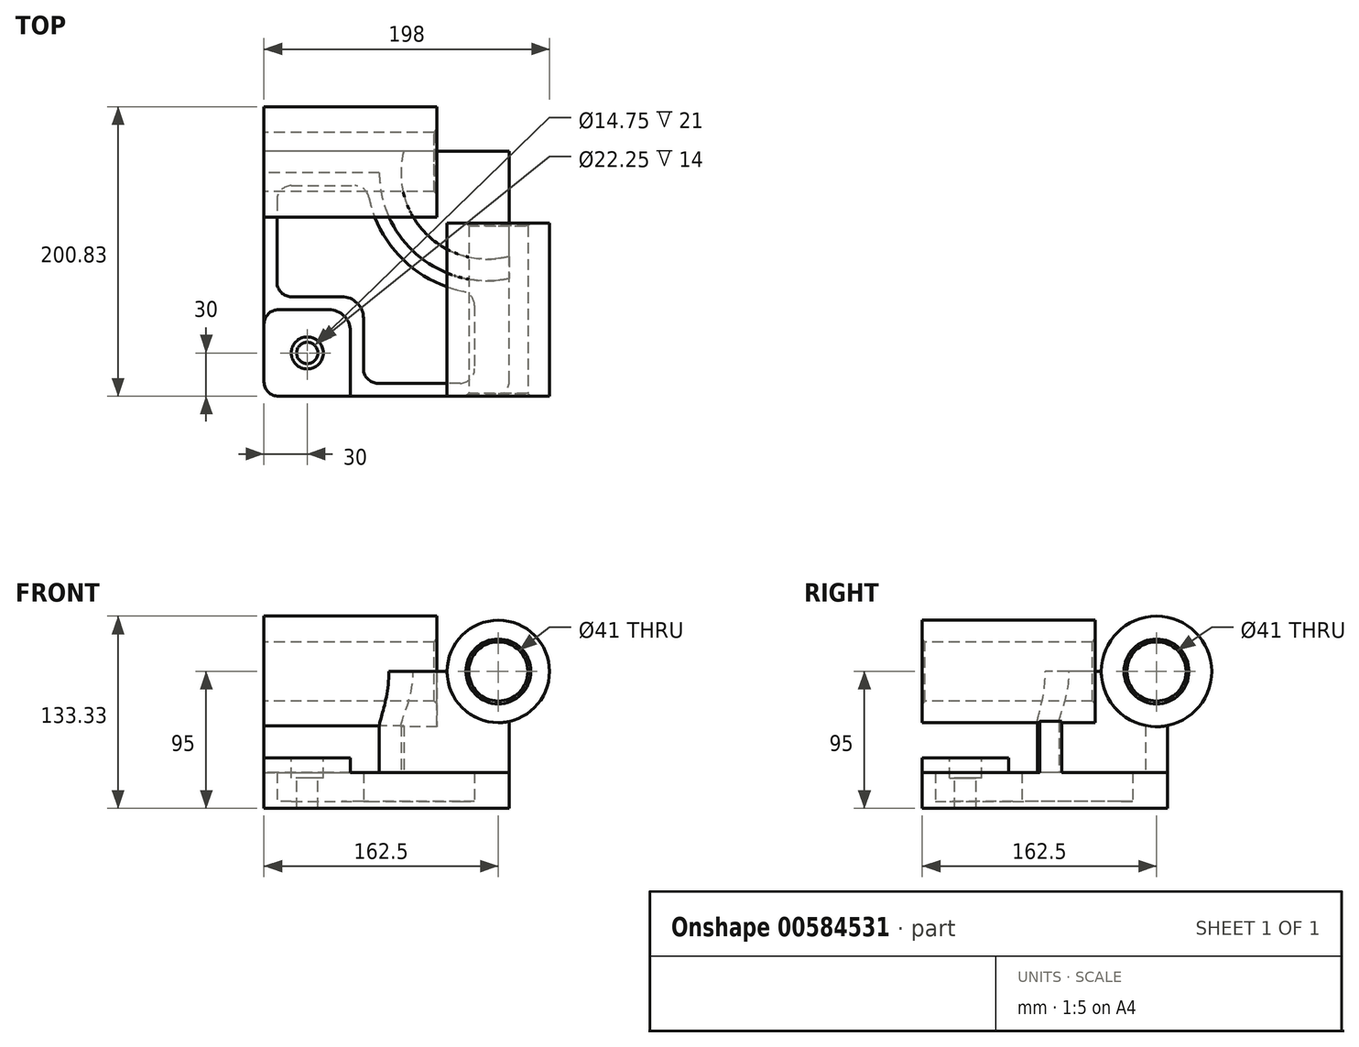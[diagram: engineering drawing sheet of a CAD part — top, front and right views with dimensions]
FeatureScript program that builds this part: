
annotation { "Feature Type Name" : "Feature", "Feature Type Description" : "" }
export const myFeature = defineFeature(function(context is Context, id is Id, definition is map)
    precondition{}
    {
        {
            var Q0;
            Q0=qCreatedBy(makeId("Top.planeOp"),FACE);
            var sketch = newSketch(context, id + "F0", { "sketchPlane" : qUnion([Q0])});
            skLineSegment(sketch, "E0", {"start": v(0, 0) * mm, "end": v(213, 0) * mm});
            skLineSegment(sketch, "E1", {"start": v(213, 0) * mm, "end": v(213, 200) * mm});
            skLineSegment(sketch, "E2", {"start": v(213, 200) * mm, "end": v(0, 200) * mm});
            skLineSegment(sketch, "E3", {"start": v(0, 200) * mm, "end": v(0, 0) * mm});
            skLineSegment(sketch, "E4", {"start": v(0, 0) * mm, "end": v(60, 0) * mm});
            skLineSegment(sketch, "E5", {"start": v(60, 0) * mm, "end": v(60, 60) * mm});
            skLineSegment(sketch, "E6", {"start": v(60, 60) * mm, "end": v(0, 60) * mm});
            skLineSegment(sketch, "E7", {"start": v(0, 0) * mm, "end": v(170, 0) * mm});
            skLineSegment(sketch, "E8", {"start": v(170, 0) * mm, "end": v(170, 170) * mm});
            skLineSegment(sketch, "E9", {"start": v(170, 170) * mm, "end": v(0, 170) * mm});
            skLineSegment(sketch, "E10", {"start": v(170, 0) * mm, "end": v(155, 0) * mm});
            skLineSegment(sketch, "E11", {"start": v(155, 0) * mm, "end": v(155, 80) * mm});
            skLineSegment(sketch, "E12", {"start": v(0, 155) * mm, "end": v(80, 155) * mm});
            skLineSegment(sketch, "E13", {"start": v(9, 146) * mm, "end": v(71.48, 146) * mm});
            skLineSegment(sketch, "E14", {"start": v(146, 71.48) * mm, "end": v(146, 9) * mm});
            skLineSegment(sketch, "E15", {"start": v(146, 9) * mm, "end": v(69, 9) * mm});
            skLineSegment(sketch, "E16", {"start": v(69, 9) * mm, "end": v(69, 69) * mm});
            skLineSegment(sketch, "E17", {"start": v(9, 146) * mm, "end": v(9, 69) * mm});
            skLineSegment(sketch, "E18", {"start": v(9, 69) * mm, "end": v(69, 69) * mm});
            skArc(sketch, "E19", {"start": v(80, 155) * mm, "mid": v(107.57, 96.9) * mm, "end": v(170, 81.52) * mm});
            skArc(sketch, "E20", {"start": v(71.48, 146) * mm, "mid": v(95.6, 95.6) * mm, "end": v(146, 71.48) * mm});
            skArc(sketch, "E21", {"start": v(96.9, 170) * mm, "mid": v(112.57, 112.57) * mm, "end": v(170, 96.9) * mm});
            skSolve(sketch);
        }
        {
            var Q0;
            {var subQ4=sQuery(id+"F0.wireOp",EDGE,"E5");Q0=makeQuery(id+"F0.imprint","IMPRINT",FACE,{"disambiguationData":[TD([[makeQuery(id+"F0.imprint","IMPRINT",EDGE,{"derivedFrom":subQ4}),1.0]])]});}
            extrude(context, id + "F1", {"entities" : qUnion([Q0]), "depth" : 35 * mm, "offsetDistance" : 25 * mm});
        }
        {
            var Q0;
            {var subQ6=sQuery(id+"F0.wireOp",EDGE,"E5");Q0=makeQuery(id+"F0.imprint","IMPRINT",FACE,{"disambiguationData":[TD([[makeQuery(id+"F0.imprint","IMPRINT",EDGE,{"derivedFrom":subQ6}),-1.0]])]});}
            extrude(context, id + "F2", {"entities" : qUnion([Q0]), "operationType" : NewBodyOperationType.ADD, "depth" : 25 * mm, "offsetDistance" : 25 * mm});
        }
        {
            var Q0;
            {var subQ0=sQuery(id+"F0.wireOp",EDGE,"E12");Q0=makeQuery(id+"F0.imprint","IMPRINT",FACE,{"disambiguationData":[TD([[makeQuery(id+"F0.imprint","IMPRINT",EDGE,{"derivedFrom":subQ0}),1.0]])]});}
            var Q1;
            {var subQ0=sQuery(id+"F0.wireOp",EDGE,"E10");Q1=makeQuery(id+"F0.imprint","IMPRINT",FACE,{"disambiguationData":[TD([[makeQuery(id+"F0.imprint","IMPRINT",EDGE,{"derivedFrom":subQ0}),-1.0]])]});}
            extrude(context, id + "F3", {"entities" : qUnion([Q0, Q1]), "operationType" : NewBodyOperationType.ADD, "depth" : 95 * mm, "offsetDistance" : 25 * mm});
        }
        {
            var Q0;
            Q0=makeQuery(id+"F0.imprint","IMPRINT",FACE,{"disambiguationData":[TD([[makeQuery(id+"F0.imprint","IMPRINT",EDGE,{"derivedFrom":sQuery(id+"F0.wireOp",EDGE,"E13")}),-1.0]])]});
            extrude(context, id + "F4", {"entities" : qUnion([Q0]), "operationType" : NewBodyOperationType.ADD, "depth" : 5 * mm, "offsetDistance" : 25 * mm});
        }
        {
            var Q0;
            {var subQ10=sQuery(id+"F0.wireOp",EDGE,"E0");Q0=makeQuery(id+"F0.imprint","IMPRINT",FACE,{"disambiguationData":[TD([[makeQuery(id+"F0.imprint","IMPRINT",EDGE,{"derivedFrom":subQ10}),1.0]])]});}
            var Q1;
            {var subQ3=sQuery(id+"F0.wireOp",EDGE,"E21");Q1=makeQuery(id+"F0.imprint","IMPRINT",FACE,{"disambiguationData":[TD([[makeQuery(id+"F0.imprint","IMPRINT",EDGE,{"derivedFrom":subQ3}),1.0]])]});}
            extrude(context, id + "F5", {"entities" : qUnion([Q0, Q1]), "operationType" : NewBodyOperationType.ADD, "depth" : 25 * mm, "offsetDistance" : 25 * mm});
        }
        {
            var Q0;
            Q0=qCreatedBy(makeId("Front.planeOp"),FACE);
            var sketch = newSketch(context, id + "F6", { "sketchPlane" : qUnion([Q0])});
            skLineSegment(sketch, "E22.0.0", {"start": v(0, 0) * mm, "end": v(213, 0) * mm});
            skLineSegment(sketch, "E22.0.1", {"start": v(213, 0) * mm, "end": v(213, 25) * mm});
            skLineSegment(sketch, "E22.0.2", {"start": v(213, 25) * mm, "end": v(170, 25) * mm});
            skLineSegment(sketch, "E22.0.3", {"start": v(170, 25) * mm, "end": v(170, 95) * mm});
            skLineSegment(sketch, "E22.0.4", {"start": v(170, 95) * mm, "end": v(155, 95) * mm});
            skLineSegment(sketch, "E22.0.5", {"start": v(155, 95) * mm, "end": v(155, 25) * mm});
            skLineSegment(sketch, "E22.0.6", {"start": v(155, 25) * mm, "end": v(60, 25) * mm});
            skLineSegment(sketch, "E22.0.7", {"start": v(60, 25) * mm, "end": v(60, 35) * mm});
            skLineSegment(sketch, "E22.0.8", {"start": v(60, 35) * mm, "end": v(0, 35) * mm});
            skLineSegment(sketch, "E22.0.9", {"start": v(0, 35) * mm, "end": v(0, 0) * mm});
            skPoint(sketch, "E23", {"position": v(162.5, 95) * mm});
            skCircle(sketch, "E24", {"center": v(162.5, 95) * mm, "radius": 20.5 * mm});
            skCircle(sketch, "E25", {"center": v(162.5, 95) * mm, "radius": 35.5 * mm});
            skSolve(sketch);
        }
        {
            var Q0;
            {var subQ0=sQuery(id+"F6.wireOp",EDGE,"E25");var subQ1=sQuery(id+"F6.wireOp",EDGE,"E22.0.3");var subQ2=makeQuery(id+"F6.imprint","INTERSECT",VERTEX,{"derivedFrom":[subQ1,subQ0]});Q0=makeQuery(id+"F6.imprint","IMPRINT",FACE,{"disambiguationData":[TD([[makeQuery(id+"F6.imprint","IMPRINT",EDGE,{"disambiguationData":[TD([[subQ2,-1.0]])],"derivedFrom":subQ1}),-1.0]])]});}
            var Q1;
            {var subQ0=sQuery(id+"F6.wireOp",EDGE,"E25");var subQ1=sQuery(id+"F6.wireOp",EDGE,"E22.0.3");var subQ2=makeQuery(id+"F6.imprint","INTERSECT",VERTEX,{"derivedFrom":[subQ1,subQ0]});Q1=makeQuery(id+"F6.imprint","IMPRINT",FACE,{"disambiguationData":[TD([[makeQuery(id+"F6.imprint","IMPRINT",EDGE,{"disambiguationData":[TD([[subQ2,-1.0]])],"derivedFrom":subQ1}),1.0]])]});}
            extrude(context, id + "F7", {"entities" : qUnion([Q0, Q1]), "operationType" : NewBodyOperationType.ADD, "oppositeDirection" : true, "depth" : 120 * mm, "offsetDistance" : 25 * mm});
        }
        {
            var Q0;
            {var subQ0=sQuery(id+"F6.wireOp",EDGE,"E22.0.4");Q0=makeQuery(id+"F6.imprint","IMPRINT",FACE,{"disambiguationData":[TD([[makeQuery(id+"F6.imprint","IMPRINT",EDGE,{"derivedFrom":subQ0}),-1.0]])]});}
            var Q1;
            {var subQ0=sQuery(id+"F6.wireOp",EDGE,"E22.0.4");Q1=makeQuery(id+"F6.imprint","IMPRINT",FACE,{"disambiguationData":[TD([[makeQuery(id+"F6.imprint","IMPRINT",EDGE,{"derivedFrom":subQ0}),1.0]])]});}
            extrude(context, id + "F8", {"entities" : qUnion([Q0, Q1]), "operationType" : NewBodyOperationType.REMOVE, "oppositeDirection" : true, "depth" : 120 * mm, "offsetDistance" : 25 * mm});
        }
        {
            var Q0;
            Q0=qCreatedBy(makeId("Right.planeOp"),FACE);
            var sketch = newSketch(context, id + "F9", { "sketchPlane" : qUnion([Q0])});
            skLineSegment(sketch, "E26.0.0", {"start": v(200, 0) * mm, "end": v(0, 0) * mm});
            skLineSegment(sketch, "E26.0.1", {"start": v(0, 0) * mm, "end": v(0, 35) * mm});
            skLineSegment(sketch, "E26.0.2", {"start": v(0, 35) * mm, "end": v(60, 35) * mm});
            skLineSegment(sketch, "E26.0.3", {"start": v(60, 35) * mm, "end": v(60, 25) * mm});
            skLineSegment(sketch, "E26.0.4", {"start": v(60, 25) * mm, "end": v(155, 25) * mm});
            skLineSegment(sketch, "E26.0.5", {"start": v(155, 25) * mm, "end": v(155, 95) * mm});
            skLineSegment(sketch, "E26.0.6", {"start": v(155, 95) * mm, "end": v(170, 95) * mm});
            skLineSegment(sketch, "E26.0.7", {"start": v(170, 95) * mm, "end": v(170, 25) * mm});
            skLineSegment(sketch, "E26.0.8", {"start": v(170, 25) * mm, "end": v(200, 25) * mm});
            skLineSegment(sketch, "E26.0.9", {"start": v(200, 25) * mm, "end": v(200, 0) * mm});
            skPoint(sketch, "E27", {"position": v(162.5, 95) * mm});
            skCircle(sketch, "E28", {"center": v(162.5, 95) * mm, "radius": 20.5 * mm});
            skCircle(sketch, "E29", {"center": v(162.5, 95) * mm, "radius": 38.33 * mm});
            skSolve(sketch);
        }
        {
            var Q0;
            {var subQ0=sQuery(id+"F9.wireOp",EDGE,"E29");var subQ1=sQuery(id+"F9.wireOp",EDGE,"E26.0.5");var subQ2=makeQuery(id+"F9.imprint","INTERSECT",VERTEX,{"derivedFrom":[subQ1,subQ0]});Q0=makeQuery(id+"F9.imprint","IMPRINT",FACE,{"disambiguationData":[TD([[makeQuery(id+"F9.imprint","IMPRINT",EDGE,{"disambiguationData":[TD([[subQ2,-1.0]])],"derivedFrom":subQ1}),1.0]])]});}
            var Q1;
            {var subQ0=sQuery(id+"F9.wireOp",EDGE,"E29");var subQ1=sQuery(id+"F9.wireOp",EDGE,"E26.0.5");var subQ2=makeQuery(id+"F9.imprint","INTERSECT",VERTEX,{"derivedFrom":[subQ1,subQ0]});Q1=makeQuery(id+"F9.imprint","IMPRINT",FACE,{"disambiguationData":[TD([[makeQuery(id+"F9.imprint","IMPRINT",EDGE,{"disambiguationData":[TD([[subQ2,-1.0]])],"derivedFrom":subQ1}),-1.0]])]});}
            extrude(context, id + "F10", {"entities" : qUnion([Q0, Q1]), "operationType" : NewBodyOperationType.ADD, "depth" : 120 * mm, "offsetDistance" : 25 * mm});
        }
        {
            var Q0;
            {var subQ0=sQuery(id+"F9.wireOp",EDGE,"E26.0.6");Q0=makeQuery(id+"F9.imprint","IMPRINT",FACE,{"disambiguationData":[TD([[makeQuery(id+"F9.imprint","IMPRINT",EDGE,{"derivedFrom":subQ0}),1.0]])]});}
            var Q1;
            {var subQ0=sQuery(id+"F9.wireOp",EDGE,"E26.0.6");Q1=makeQuery(id+"F9.imprint","IMPRINT",FACE,{"disambiguationData":[TD([[makeQuery(id+"F9.imprint","IMPRINT",EDGE,{"derivedFrom":subQ0}),-1.0]])]});}
            extrude(context, id + "F11", {"entities" : qUnion([Q0, Q1]), "operationType" : NewBodyOperationType.REMOVE, "depth" : 120 * mm, "offsetDistance" : 25 * mm});
        }
        {
            var Q0;
            Q0=makeQuery(id+"F5.opExtrude","SWEPT_EDGE",EDGE,{"disambiguationData":[OSD([sQuery(id+"F0.wireOp",EDGE,"E0"),sQuery(id+"F0.wireOp",EDGE,"E1")])]});
            var Q1;
            Q1=makeQuery(id+"F5.opExtrude","SWEPT_EDGE",EDGE,{"disambiguationData":[OSD([sQuery(id+"F0.wireOp",EDGE,"E1"),sQuery(id+"F0.wireOp",EDGE,"E2")])]});
            var Q2;
            Q2=makeQuery(id+"F5.opExtrude","SWEPT_EDGE",EDGE,{"disambiguationData":[OSD([sQuery(id+"F0.wireOp",EDGE,"E2"),sQuery(id+"F0.wireOp",EDGE,"E3")])]});
            var Q3;
            Q3=makeQuery(id+"F1.opExtrude","SWEPT_EDGE",EDGE,{"disambiguationData":[OSD([sQuery(id+"F0.wireOp",EDGE,"E3"),sQuery(id+"F0.wireOp",EDGE,"E7")])]});
            fillet(context, id + "F12", {"entities" : qUnion([Q0, Q1, Q2, Q3]), "radius" : 10 * mm, "tangentPropagation" : true, "allowEdgeOverflow" : false});
        }
        {
            var Q0;
            Q0=makeQuery(id+"F1.opExtrude","SWEPT_EDGE",EDGE,{"disambiguationData":[OSD([sQuery(id+"F0.wireOp",EDGE,"E5"),sQuery(id+"F0.wireOp",EDGE,"E6")])]});
            var Q1;
            Q1=makeQuery(id+"F2.opExtrude","SWEPT_EDGE",EDGE,{"disambiguationData":[OSD([sQuery(id+"F0.wireOp",EDGE,"E16"),sQuery(id+"F0.wireOp",EDGE,"E18")])]});
            fillet(context, id + "F13", {"entities" : qUnion([Q0, Q1]), "radius" : 15 * mm, "tangentPropagation" : true, "allowEdgeOverflow" : false});
        }
        {
            var Q0;
            Q0=makeQuery(id+"F2.opExtrude","SWEPT_EDGE",EDGE,{"disambiguationData":[OSD([sQuery(id+"F0.wireOp",EDGE,"E13"),sQuery(id+"F0.wireOp",EDGE,"E20")])]});
            var Q1;
            Q1=makeQuery(id+"F2.opExtrude","SWEPT_EDGE",EDGE,{"disambiguationData":[OSD([sQuery(id+"F0.wireOp",EDGE,"E13"),sQuery(id+"F0.wireOp",EDGE,"E17")])]});
            var Q2;
            Q2=makeQuery(id+"F2.opExtrude","SWEPT_EDGE",EDGE,{"disambiguationData":[OSD([sQuery(id+"F0.wireOp",EDGE,"E17"),sQuery(id+"F0.wireOp",EDGE,"E18")])]});
            var Q3;
            Q3=makeQuery(id+"F2.opExtrude","SWEPT_EDGE",EDGE,{"disambiguationData":[OSD([sQuery(id+"F0.wireOp",EDGE,"E15"),sQuery(id+"F0.wireOp",EDGE,"E16")])]});
            var Q4;
            Q4=makeQuery(id+"F2.opExtrude","SWEPT_EDGE",EDGE,{"disambiguationData":[OSD([sQuery(id+"F0.wireOp",EDGE,"E14"),sQuery(id+"F0.wireOp",EDGE,"E20")])]});
            var Q5;
            Q5=makeQuery(id+"F2.opExtrude","SWEPT_EDGE",EDGE,{"disambiguationData":[OSD([sQuery(id+"F0.wireOp",EDGE,"E14"),sQuery(id+"F0.wireOp",EDGE,"E15")])]});
            fillet(context, id + "F14", {"entities" : qUnion([Q0, Q1, Q2, Q3, Q4, Q5]), "radius" : 10 * mm, "tangentPropagation" : true, "allowEdgeOverflow" : false});
        }
        {
            var Q0;
            Q0=qCreatedBy(makeId("Top.planeOp"),FACE);
            cPlane(context, id + "F15", {"entities" : qUnion([Q0]), "cplaneType" : CPlaneType.OFFSET, "offset" : 35 * mm, "width" : 150 * mm, "height" : 150 * mm});
        }
        {
            var Q0;
            Q0=qCreatedBy(id+"F15.planeOp",FACE);
            var sketch = newSketch(context, id + "F16", { "sketchPlane" : qUnion([Q0])});
            skLineSegment(sketch, "E30", {"start": v(0, 0) * mm, "end": v(60, 0) * mm});
            skLineSegment(sketch, "E31", {"start": v(60, 0) * mm, "end": v(60, 60) * mm});
            skLineSegment(sketch, "E32", {"start": v(60, 60) * mm, "end": v(0, 60) * mm});
            skLineSegment(sketch, "E33", {"start": v(0, 60) * mm, "end": v(0, 0) * mm});
            skLineSegment(sketch, "E34", {"start": v(0, 0) * mm, "end": v(60, 60) * mm});
            skPoint(sketch, "E35", {"position": v(30, 30) * mm});
            skSolve(sketch);
        }
        {
            var Q0;
            Q0=sQuery(id+"F16.wireOp",VERTEX,"E35");
            var Q1;
            Q1=makeQuery(id+"F1.opExtrude","SWEPT_BODY",BODY,{"disambiguationData":[OSD([sQuery(id+"F0.wireOp",EDGE,"E3"),sQuery(id+"F0.wireOp",EDGE,"E5"),sQuery(id+"F0.wireOp",EDGE,"E6"),sQuery(id+"F0.wireOp",EDGE,"E7")])]});
            hole(context, id + "F17", {"style" : HoleStyle.C_BORE, "endStyle" : HoleEndStyle.THROUGH, "standardTappedOrClearance" : lookupTablePath({ "standard" : "ISO", "fit" : "Close", "size" : "M14", "type" : "Clearance" }), "standardBlindInLast" : lookupTablePath({ "fit" : "Close", "standard" : "ISO", "size" : "M14", "type" : "Clearance" }), "holeDiameter" : 14.75 * mm, "cBoreDiameter" : 22.25 * mm, "cBoreDepth" : 14 * mm, "majorDiameter" : 5 * mm, "isTappedThrough" : true, "tappedDepth" : 12 * mm, "tapClearance" : 3, "startFromSketch" : true, "locations" : qUnion([Q0]), "scope" : qUnion([Q1])});
        }
        {
            var Q0;
            {var subQ0=sQuery(id+"F9.wireOp",EDGE,"E28");Q0=makeQuery(id+"F11.boolean.opBoolean","MERGE",EDGE,{"derivedFrom":[makeQuery(id+"F10.opExtrude","CAP_EDGE",EDGE,{"disambiguationData":[OSD([subQ0])],"isStart":true}),makeQuery(id+"F11.opExtrude","CAP_EDGE",EDGE,{"disambiguationData":[OSD([subQ0])],"isStart":true})]});}
            var Q1;
            {var subQ0=sQuery(id+"F6.wireOp",EDGE,"E24");Q1=makeQuery(id+"F8.boolean.opBoolean","MERGE",EDGE,{"derivedFrom":[makeQuery(id+"F7.opExtrude","CAP_EDGE",EDGE,{"disambiguationData":[OSD([subQ0])],"isStart":true}),makeQuery(id+"F8.opExtrude","CAP_EDGE",EDGE,{"disambiguationData":[OSD([subQ0])],"isStart":true})]});}
            var Q2;
            Q2=makeQuery(id+"F10.opExtrude","CAP_EDGE",EDGE,{"disambiguationData":[OSD([sQuery(id+"F9.wireOp",EDGE,"E28")])],"isStart":false});
            var Q3;
            Q3=makeQuery(id+"F7.opExtrude","CAP_EDGE",EDGE,{"disambiguationData":[OSD([sQuery(id+"F6.wireOp",EDGE,"E24")])],"isStart":false});
            chamfer(context, id + "F18", {"entities" : qUnion([Q0, Q1, Q2, Q3]), "chamferType" : ChamferType.OFFSET_ANGLE, "width" : 2 * mm, "oppositeDirection" : false, "angle" : 45 * degree, "tangentPropagation" : true});
        }
    });
